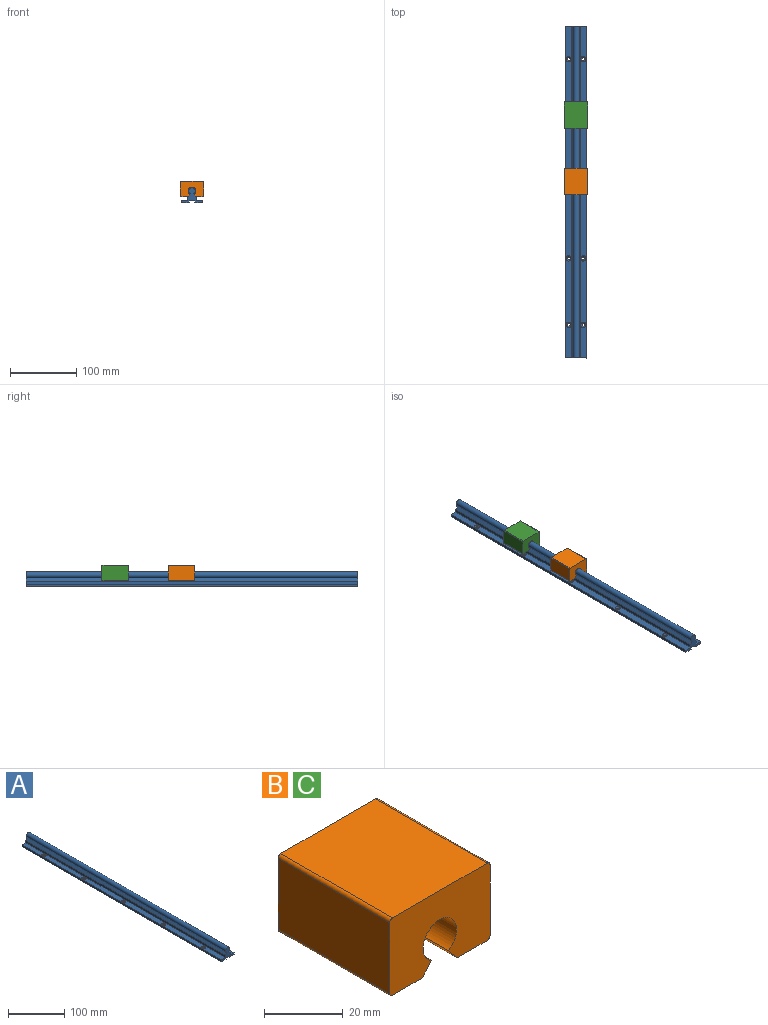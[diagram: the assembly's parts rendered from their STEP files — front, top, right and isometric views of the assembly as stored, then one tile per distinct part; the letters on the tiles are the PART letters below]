
ASSEMBLY  parts=3 mates=2
PART A: 36 faces, bbox 32x500x23 mm
  f0: plane 32x23mm, normal (0,-1,0), area 281.5mm2, adj f1,f2,f3,f4,f5,f6,f7,f8
  f1: plane 500x9.8mm, normal (0,0,1), area 4648.7mm2, adj f0,f2,f14,f15,f17,f23,f25,f29
  f2: plane 500x4.9mm, normal (1,0,0), area 2450mm2, adj f0,f1,f3,f15
  f3: plane 500x4.69mm, normal (0.77,0,0.63), area 3032.6mm2, adj f0,f2,f4,f15
  f4: cylinder r=5mm len=500mm, axis (0,1,0), area 13261.5mm2, adj f0,f3,f5,f15
  f5: plane 500x4.69mm, normal (-0.77,0,0.63), area 3032.6mm2, adj f0,f4,f6,f15
  f6: plane 500x4.9mm, normal (-1,0,0), area 2450mm2, adj f0,f5,f7,f15
  f7: plane 500x9.8mm, normal (0,0,1), area 4648.7mm2, adj f0,f6,f8,f15,f19,f21,f27,f31
  f8: plane 500x4mm, normal (-1,0,0), area 2000mm2, adj f0,f7,f9,f15
  f9: plane 500x12mm, normal (0,0,-1), area 5920.5mm2, adj f0,f8,f10,f15,f18,f20,f26,f30
  f10: plane 500x3mm, normal (1,0,0), area 1500mm2, adj f0,f9,f11,f15
  f11: plane 500x8mm, normal (0,0,-1), area 4000mm2, adj f0,f10,f12,f15
  f12: plane 500x3mm, normal (-1,0,0), area 1500mm2, adj f0,f11,f13,f15
  f13: plane 500x12mm, normal (0,0,-1), area 5920.5mm2, adj f0,f12,f14,f15,f16,f22,f24,f28
  f14: plane 500x4mm, normal (1,0,0), area 2000mm2, adj f0,f1,f13,f15
  f15: plane 32x23mm, normal (0,1,0), area 281.5mm2, adj f1,f2,f3,f4,f5,f6,f7,f8
  f16: cylinder r=2.25mm len=4.5mm, axis (0,0,1), area 31.8mm2, adj f13,f17
  f17: cone r=2.25mm half-angle=45deg, axis (0,0,1), area 48.6mm2, adj f1,f16
  f18: cylinder r=2.25mm len=4.5mm, axis (0,0,1), area 31.8mm2, adj f9,f19
  f19: cone r=2.25mm half-angle=45deg, axis (0,0,1), area 48.6mm2, adj f7,f18
  f20: cylinder r=2.25mm len=4.5mm, axis (0,0,1), area 31.8mm2, adj f9,f21
  f21: cone r=2.25mm half-angle=45deg, axis (0,0,1), area 48.6mm2, adj f7,f20
  f22: cylinder r=2.25mm len=4.5mm, axis (0,0,1), area 31.8mm2, adj f13,f23
  f23: cone r=2.25mm half-angle=45deg, axis (0,0,1), area 48.6mm2, adj f1,f22
  f24: cylinder r=2.25mm len=4.5mm, axis (0,0,1), area 31.8mm2, adj f13,f25
  f25: cone r=2.25mm half-angle=45deg, axis (0,0,1), area 48.6mm2, adj f1,f24
  f26: cylinder r=2.25mm len=4.5mm, axis (0,0,1), area 31.8mm2, adj f9,f27
  f27: cone r=2.25mm half-angle=45deg, axis (0,0,1), area 48.6mm2, adj f7,f26
  f28: cylinder r=2.25mm len=4.5mm, axis (0,0,1), area 31.8mm2, adj f13,f29
  f29: cone r=2.25mm half-angle=45deg, axis (0,0,1), area 48.6mm2, adj f1,f28
  f30: cylinder r=2.25mm len=4.5mm, axis (0,0,1), area 31.8mm2, adj f9,f31
  f31: cone r=2.25mm half-angle=45deg, axis (0,0,1), area 48.6mm2, adj f7,f30
  f32: cylinder r=2.25mm len=4.5mm, axis (0,0,1), area 31.8mm2, adj f13,f33
  f33: cone r=2.25mm half-angle=45deg, axis (0,0,1), area 48.6mm2, adj f1,f32
  f34: cylinder r=2.25mm len=4.5mm, axis (0,0,1), area 31.8mm2, adj f9,f35
  f35: cone r=2.25mm half-angle=45deg, axis (0,0,1), area 48.6mm2, adj f7,f34
PART B: 16 faces, bbox 36x40x24 mm
  f0: plane 40x22mm, normal (-1,0,0), area 880mm2, adj f1,f13,f14,f15
  f1: cylinder r=1mm len=40mm, axis (0,1,0), area 62.8mm2, adj f0,f2,f14,f15
  f2: plane 40x10.34mm, normal (0,0,-1), area 413.7mm2, adj f1,f3,f14,f15
  f3: cylinder r=1mm len=40mm, axis (0,1,0), area 34.9mm2, adj f2,f4,f14,f15
  f4: plane 40x3.45mm, normal (0.77,0,-0.64), area 180mm2, adj f3,f5,f14,f15
  f5: cylinder r=6mm len=40mm, axis (0,1,0), area 1256.6mm2, adj f4,f6,f14,f15
  f6: plane 40x3.45mm, normal (-0.77,0,-0.64), area 180mm2, adj f5,f7,f14,f15
  f7: cylinder r=1mm len=40mm, axis (0,1,0), area 34.9mm2, adj f6,f8,f14,f15
  f8: plane 40x10.34mm, normal (0,0,-1), area 413.7mm2, adj f7,f9,f14,f15
  f9: cylinder r=1mm len=40mm, axis (0,1,0), area 62.8mm2, adj f8,f10,f14,f15
  f10: plane 40x22mm, normal (1,0,0), area 880mm2, adj f9,f11,f14,f15
  f11: cylinder r=1mm len=40mm, axis (0,1,0), area 62.8mm2, adj f10,f12,f14,f15
  f12: plane 40x34mm, normal (0,0,1), area 1360mm2, adj f11,f13,f14,f15
  f13: cylinder r=1mm len=40mm, axis (0,1,0), area 62.8mm2, adj f0,f12,f14,f15
  f14: plane 36x24mm, normal (0,-1,0), area 718.3mm2, adj f0,f1,f2,f3,f4,f5,f6,f7
  f15: plane 36x24mm, normal (0,1,0), area 718.3mm2, adj f0,f1,f2,f3,f4,f5,f6,f7
PART C: same geometry as B
PLACE A t=(-20.59,-201.95,-185.51)mm
PLACE B t=(-20.59,-416.34,-172.71)mm
PLACE C t=(-20.59,-316.34,-172.71)mm
MATE slider A.f4 <-> B.f5  axis (0,1,0) through (-20.59,-451.95,-167.51)mm
MATE fastened B.f12 <-> C.f12  axis (0,0,1) through (-20.59,-436.34,-152.51)mm
